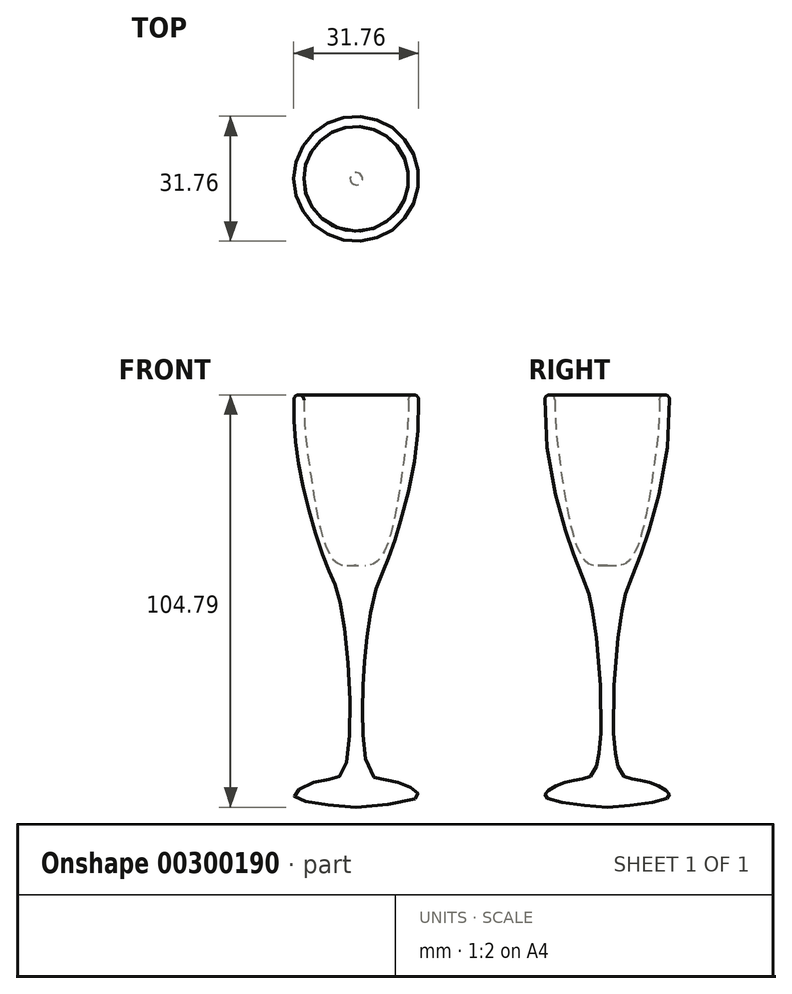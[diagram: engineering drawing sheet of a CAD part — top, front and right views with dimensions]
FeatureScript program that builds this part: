
annotation { "Feature Type Name" : "Feature", "Feature Type Description" : "" }
export const myFeature = defineFeature(function(context is Context, id is Id, definition is map)
    precondition{}
    {
        {
            var Q0;
            Q0=qCreatedBy(makeId("Front.planeOp"),FACE);
            var sketch = newSketch(context, id + "F0", { "sketchPlane" : qUnion([Q0])});
            skLineSegment(sketch, "E0", {"start": v(-8.95, 65.77) * mm, "end": v(-10.97, 65.77) * mm});
            skFitSpline(sketch, "E1", {"points": [v(-10.97, 65.77) * mm, v(-14.1, 51.87) * mm, v(-15.87, 33.66) * mm, v(-13.9, 14.08) * mm, v(-7.64, -7.06) * mm, v(-3.71, -19.07) * mm, v(-3.28, -59.95) * mm, v(-8.77, -62.15) * mm, v(-15.8, -65.88) * mm, v(0, -68.96) * mm], "startDerivative": vector(-32.58, -128.68) * mm, "endDerivative": vector(216, -17) * mm});
            skLineSegment(sketch, "E2", {"start": v(0, 65.77) * mm, "end": v(0, -68.96) * mm});
            skPoint(sketch, "E3.orphan", {"position": v(0, 75.85) * mm});
            skLineSegment(sketch, "E4", {"start": v(0, 65.77) * mm, "end": v(0, -68.96) * mm, "construction": true});
            skPoint(sketch, "E5.4.internal.snap0", {"position": v(-5.49, 65.77) * mm});
            skFitSpline(sketch, "E5", {"points": [v(-8.95, 65.77) * mm, v(-12.06, 50.6) * mm, v(-13.3, 33.04) * mm, v(-11.44, 14.55) * mm, v(-5.49, -6.42) * mm, v(0, -7.33) * mm], "startDerivative": vector(-17.06, -73) * mm, "endDerivative": vector(48.4, 7.45) * mm});
            skSolve(sketch);
        }
        {
            var Q0;
            Q0=makeQuery(id+"F0.imprint","IMPRINT",FACE,{"disambiguationData":[TD([[makeQuery(id+"F0.imprint","IMPRINT",EDGE,{"derivedFrom":sQuery(id+"F0.wireOp",EDGE,"E0")}),1.0]])]});
            var Q1;
            Q1=sQuery(id+"F0.wireOp",EDGE,"E2");
            revolve(context, id + "F1", {"entities" : qUnion([Q0]), "axis" : qUnion([Q1]), "revolveType" : RevolveType.FULL});
        }
        {
            var Q0;
            Q0=makeQuery(id+"F1.opRevolve","SWEPT_EDGE",EDGE,{"disambiguationData":[OSD([sQuery(id+"F0.wireOp",EDGE,"E0"),sQuery(id+"F0.wireOp",EDGE,"E1")])]});
            fillet(context, id + "F2", {"entities" : qUnion([Q0]), "radius" : 5.08 * mm, "tangentPropagation" : true, "allowEdgeOverflow" : false});
        }
        {
            var Q0;
            Q0=makeQuery(id+"F2.opFillet","BLEND_EDGE",EDGE,{"blendedFrom":[makeQuery(id+"F1.opRevolve","SWEPT_EDGE",EDGE,{"disambiguationData":[OSD([sQuery(id+"F0.wireOp",EDGE,"E0"),sQuery(id+"F0.wireOp",EDGE,"E1")])]}),makeQuery(id+"F1.opRevolve","SWEPT_FACE",FACE,{"disambiguationData":[OSD([sQuery(id+"F0.wireOp",EDGE,"E5")])]})],"blendedInto":[makeQuery(id+"F1.opRevolve","SWEPT_FACE",FACE,{"disambiguationData":[OSD([sQuery(id+"F0.wireOp",EDGE,"E5")])]})]});
            fillet(context, id + "F3", {"entities" : qUnion([Q0]), "radius" : 1.27 * mm, "tangentPropagation" : true, "allowEdgeOverflow" : false});
        }
    });
